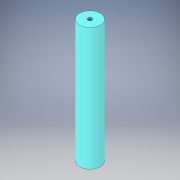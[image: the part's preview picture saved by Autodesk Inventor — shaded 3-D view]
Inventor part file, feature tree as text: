
AUTODESK INVENTOR PART (.ipt)
format: ipt  version: 2018 (Build 220112000, 112)  size: 115,712 bytes
history: native  units: in
note: dims shown in document units (in); Inventor stores cm internally (conversion verified against a paired STEP export)
features: sketch x3, hole x2, extrude x1
ambient origin geometry x8: Origin, YZ Plane, XZ Plane, XY Plane, X Axis, Y Axis, Z Axis, Center Point
bodies: Solid1 (feature_tree)
feature tree (6):
  extrude  "Extrusion1"  Depth=5.954in TaperAngle=0.0deg
  sketch  "Sketch3"  dims[d4=0.196in d5=0.5in d6=0.375in d7=0.25in d8=0.5635in d9=0.75in d10=0.8108in d11=0.5in d12=0.196in d13=0.5in d14=0.375in d15=0.25in d16=0.5635in d17=0.75in d18=0.8108in]
  hole  "Hole1"  [1 undecoded]
  hole  "Hole2"  [1 undecoded]
  sketch  "Sketch1"  dims[d0=1.0in d1=5.954in d2=0.0in]
  sketch  "Sketch2"  dims[d3=0.25in]
note: 2 required parameter values undecoded (feature->parameter linkage not recoverable at this tier; creation-order binding heuristic only, values carry confidence <= 0.55)
